# Revit family: Sirius Rig 3x WH 150 IL + PHEX Rev A
name_source: partatom
category: Mechanical Equipment
units: mm (PartAtom-declared; Revit-internal decimal feet)

## family parameters
Always vertical = Yes
Cut with Voids When Loaded = No
OmniClass Number = 23.75.10.11.14.14
OmniClass Title = Condensing Boilers
Part Type = Normal
Room Calculation Point = No
Round Connector Dimension = Use Diameter
Shared = No
Work Plane-Based = No

## types (1)
- Boiler Rig
    6 Monthly = 0
    Access Clearance Bottom = 500 mm  [stored 1.64042 ft]
    Access Clearance Front = 600 mm
    Access Clearance Left = 20 mm  [stored 0.0656168 ft]
    Access Clearance Rear = 0 mm  [stored 0 ft]
    Access Clearance Right = 20 mm  [stored 0.0656168 ft]
    Access Clearance Top = 400 mm  [stored 1.31234 ft]
    Air Inlet Connection Size = 160 mm  [stored 0.524934 ft]
    Annually = As per attached URL O & M Manual
    BMS Links = Yes
    Bespoke Timeframe = 0
    Building Regulations Seasonal Efficiency = 97.3 %
    Burner Control Type = Modulating
    CE Mark = 0085CM0128
    Colour = BDR White (no RAL number)
    Condensate Drain Size = 40 mm  [stored 0.131234 ft]
    Condensate Drain Type = Plain
    Configuration = Cascade boilers
    Control Type = 0 - 10V, Volt free enable, Direct boiler weather compensating control system.
    Daily = 0
    Default Elevation = 0 mm  [stored 0 ft]
    Drain Connection Size = 0 mm  [stored 0 ft]
    Drain Connection Type = Threaded
    Embodied Carbon = 0
    Environmental Product Declaration = 0
    ErP Rated Efficiency at Full Load = 95.1 %
    ErP Rated Efficiency at Part Load = 97.8 %
    Expected Life = 15
    External Material = Steel
    Features = Prefabricated cascade configurations - in-line or back-to-back. Includes control panel, dosing pot, pressurisation unit, insultation and LLH or PHEX
    Finish = Powder coated
    Flow and Return Connection Size = 65 mm  [stored 0.213255 ft]
    Flow and Return Connection Type = Flanged
    Flue Connection size = 110 mm  [stored 0.360892 ft]
    Flue or Air Intake Classification = B23, C13, C33
    Frequency = 50 Hz
    Fuel Connection Size = 50 mm  [stored 0.164042 ft]
    Fuel Connection Type = Flanged
    Full Load Current = 0 A
    Fuse Rating = 5 A
    Gas Consumption rate = 45.3
    Green Guide for Specification = 0
    Gross Weight = 1280.00 kg
    Heat Exchanger Material = Stainless Steel
    Heater Operation = Condensing
    Hydraulic Resistance at 11C temperature differential = 0.0
    Hydraulic Resistance at 15C temperature differential = 0.0
    Hydraulic Resistance at 20C temperature differential = 0.4
    IK Rating = 0
    IP Rating = IPX5D
    IfcExportAs = IfcBoilerType
    IfcExportType = NOTDEFINED
    Interlocks = Yes
    Life Cycle Analysis = 0
    Location of Manufacturer = 0
    Maintenance Required 0 to 300hrs = 0
    Maintenance Required 1001 to 2000hrs = 0
    Maintenance Required 2001 to 4000hrs = 0
    Maintenance Required 301 to 600hrs = 0
    Maintenance Required 4001 to 8000hrs = 0
    Maintenance Required 601 to 1000hrs = 0
    Maintenance Required 8001 to 12000hrs = 0
    Manufacturer = Potterton Commercial
    Manufacturer Website = http://www.pottertoncommercial.co.uk
    Material Ingredient Reporting = 0
    Maximum Gas Inlet Pressure = 0.0 bar
    Maximum Oil Inlet Pressure = 0.0 bar
    Maximum Operating Pressure = 6.0 bar
    Maximum Power Consumption = 849 W
    Minimum Flow Rate at 11C temperature differential = 0.000 L/s
    Minimum Flow Rate at 15C temperature differential = 0.000 L/s
    Minimum Flow Rate at 20C temperature differential = 2.030 L/s
    Minimum Gas Inlet Pressure = 0.0 bar
    Minimum Oil Inlet Pressure = 0.0 bar
    Minimum Operating Pressure = 1.0 bar
    Minimum Power Consumption = 0 W
    Monthly = 0
    Mounting = Wall Mounted
    NOx Emissions = 17
    Nominal Gas Inlet Pressure = 0.0 bar
    Nominal Oil Inlet Pressure = 0.0 bar
    Oil Consumption rate = 0
    Operation and Maintenance Manual = https://www.pottertoncommercial.co.uk
    Optional Fuel = Gas - LPG
    Overall Height = 1996 mm  [stored 6.54856 ft]
    Overall Length = 3847 mm  [stored 12.6214 ft]
    Overall Width = 1027 mm  [stored 3.36942 ft]
    Primary Fuel = Gas - NG
    Product Literature = https://www.pottertoncommercial.co.uk
    Product Model Number = 7764105
    Product Range = 3 x Sirius Three WH 150kW Inline + PHEX Rig
    Quarterly = 0
    Rated Criteria = 50/30
    Rated Output = 450000 W
    Reference Standard = EU/2016/426 GAR,  92/42/EEC, EN 15502-1, EN15502-2-1
    Responsible Extraction of Materials = 0
    Responsible Sourcing of Materials = 0
    Safety Valve Connection Size = 20 mm  [stored 0.0656168 ft]
    Safety Valve Connection Type = Threaded
    Shape = Rectangular (Vertical)
    Shipping Weight = 0.00 kg
    Sound Pressure Level = 64
    Starting Current = 0 A
    Supply Phase = 1
    Turndown Ratio = 5:1
    Type = Space Heating
    Uniclass2015 = Pr_60_60_08
    Voltage = 230 V
    Warranty ID = See manufacturers website for warranty options and T&C's
    Water Content = 0.01 m³
    Water Treatment Required = Yes
    Weekly = 0

note: source unit labels omitted for Hydraulic Resistance at 11C temperature differential, Hydraulic Resistance at 15C temperature differential, Hydraulic Resistance at 20C temperature differential — the stored unit's dimension contradicts the parameter name (converter mislabeling)

note: [stored X ft] marks values corroborated as IEEE doubles in the binary element streams (Revit-internal decimal feet)

## geometry (parser evidence)
native form markers: Blend x2, Sweep x35
no freeform markers — native parametric forms only
